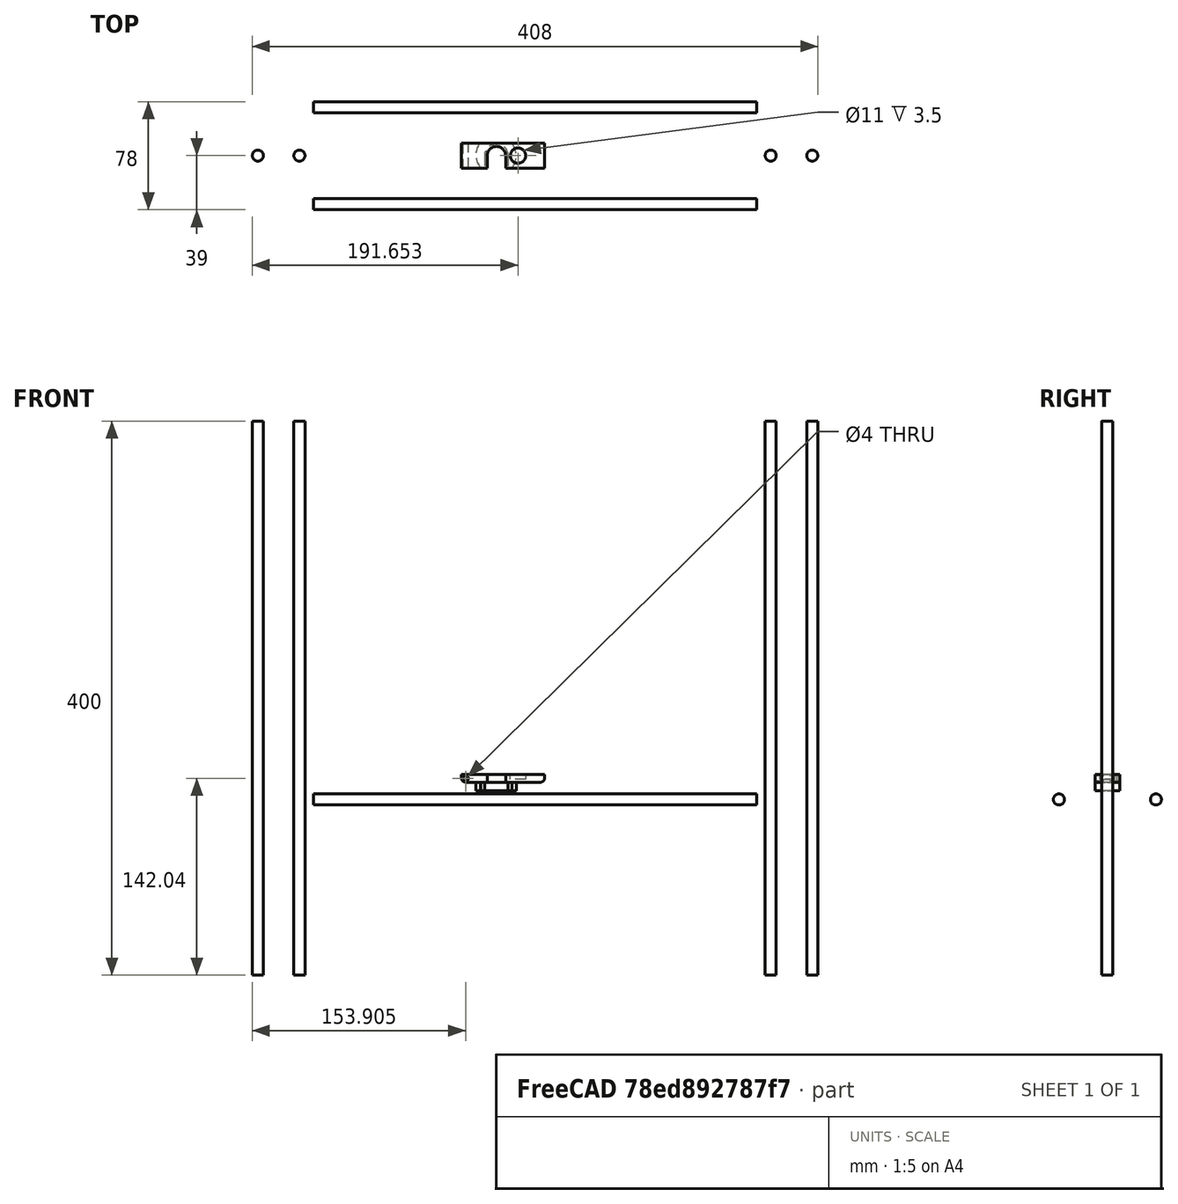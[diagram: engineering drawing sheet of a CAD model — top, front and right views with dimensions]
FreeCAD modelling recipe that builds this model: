
FCSTD DOCUMENT  (FreeCAD 0.15R4671 (Git))
Label: 3DPrinterV6
License: All rights reserved
LicenseURL: http://en.wikipedia.org/wiki/All_rights_reserved
objects: Mesh::Feature×4, PartDesign::Pad×3, Sketcher::SketchObject×2, PartDesign::Pocket×1, PartDesign::Fillet×1, Part::MultiFuse×1
note: 12 computed .brp shape members not serialized (recipe doc carries the construction recipe); baked Part::Feature solids carry a one-line shape summary decoded from their .brp

FEATURE [Sketcher::SketchObject] Sketch050
  Placement = pos=(0,0,0) rot=(0.57735,0.57735,0.57735;2.0944rad)
  sketch-geometry (2):
    g0: Circle CenterX=-35 CenterY=-23.1549 CenterZ=0 NormalX=0 NormalY=0 NormalZ=1 Radius=4
    g1: Circle CenterX=35 CenterY=-23.1549 CenterZ=0 NormalX=0 NormalY=0 NormalZ=1 Radius=4
  constraints (5):
    c: Radius(g0) = 4
    c: Equal(g0,g1)
    c: DistanceX(g0,g1) = 70
    c: DistanceX(g-1,g0) = -35
    c: DistanceY(g1,g0) = 0
FEATURE [PartDesign::Pad] Pad049  label="HorzRods"
  Length = 320
  Length2 = 100
  Midplane = true
  Placement = pos=(0,0,0) rot=(0.57735,0.57735,0.57735;2.0944rad)
  Sketch = -> Sketch050
  Type = 0
FEATURE [Sketcher::SketchObject] Sketch051
  sketch-geometry (4):
    g0: Circle CenterX=-200 CenterY=0 CenterZ=0 NormalX=0 NormalY=0 NormalZ=1 Radius=4
    g1: Circle CenterX=-170 CenterY=0 CenterZ=0 NormalX=0 NormalY=0 NormalZ=1 Radius=4
    g2: Circle CenterX=170 CenterY=0 CenterZ=0 NormalX=0 NormalY=0 NormalZ=1 Radius=4
    g3: Circle CenterX=200 CenterY=0 CenterZ=0 NormalX=0 NormalY=0 NormalZ=1 Radius=4
  constraints (12):
    c: PointOnObject(g2,g-1)
    c: Radius(g3) = 4
    c: Equal(g3,g2)
    c: Equal(g3,g1)
    c: Equal(g3,g0)
    c: DistanceY(g1,g0) = 0
    c: DistanceY(g3,g2) = 0
    c: DistanceY(g2,g1) = 0
    c: DistanceX(g0,g1) = 30
    c: DistanceX(g2,g3) = 30
    c: DistanceX(g2,g1) = -340
    c: DistanceX(g-1,g2) = 170
FEATURE [PartDesign::Pad] Pad050  label="VertRods"
  Length = 250
  Length2 = 150
  Sketch = -> Sketch051
  Type = 4
FEATURE [PartDesign::Pocket] Pocket
  Length = 3.5
  Placement = pos=(-20,8,17) rot=(0.000342,0.708549,0.705662;3.14091rad)
  Type = 0
FEATURE [Mesh::Feature] _  label="1"
  Placement = pos=(0,-35,-26) rot=(0,0,1;0rad)
FEATURE [Mesh::Feature] _002  label="3"
  Placement = pos=(-200,0,-27) rot=(0,0,1;0rad)
FEATURE [Mesh::Feature] _003  label="4"
  Placement = pos=(200,0,-28) rot=(0,0,1;3.14159rad)
FEATURE [PartDesign::Fillet] Fillet
  Base = -> Pocket [Edge14,Edge12]
  Placement = pos=(0,0,6) rot=(0,0,1;0rad)
  Radius = 3
FEATURE [PartDesign::Pad] Pad
  Length = 6
  Length2 = 100
  Placement = pos=(0,0,0) rot=(1,0,0;3.14159rad)
  Reversed = true
  Type = 0
FEATURE [Part::MultiFuse] Fusion
  Placement = pos=(-27.9,0,-16.7) rot=(0,0,1;0rad)
  Shapes = -> [Fillet,Pad]
FEATURE [Mesh::Feature] _004  label="2"
  Placement = pos=(-25.75,0,-11) rot=(0,0,1;0rad)
